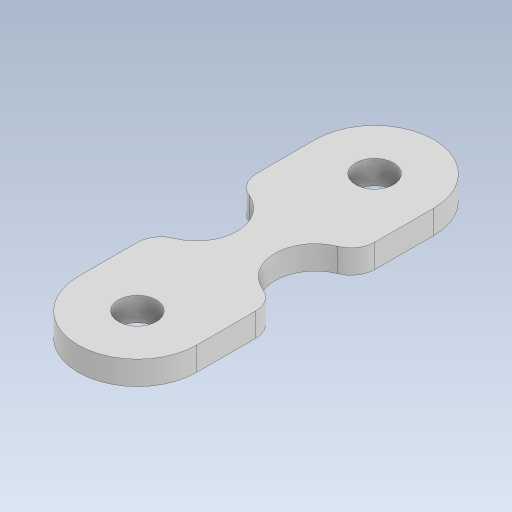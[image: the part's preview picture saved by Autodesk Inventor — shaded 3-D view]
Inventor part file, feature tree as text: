
AUTODESK INVENTOR PART (.ipt)
format: ipt  version: 2023.5 (Build 275446000, 446)  size: 294,912 bytes
history: native  units: mm
features: extrude x1, fillet x1, sketch x1
ambient origin geometry x8: Origin, YZ Plane, XZ Plane, XY Plane, X Axis, Y Axis, Z Axis, Center Point
bodies: Solid1 (feature_tree)
feature tree (3):
  extrude  "Extrusion1"  Depth=2.0mm
  fillet  "Fillet1"  Radius=20.0mm
  sketch  "Sketch1"  dims[d0=3.2mm d1=3.2mm d2=20.0mm d3=2.0mm d4=0.0mm d5=2.0mm]
